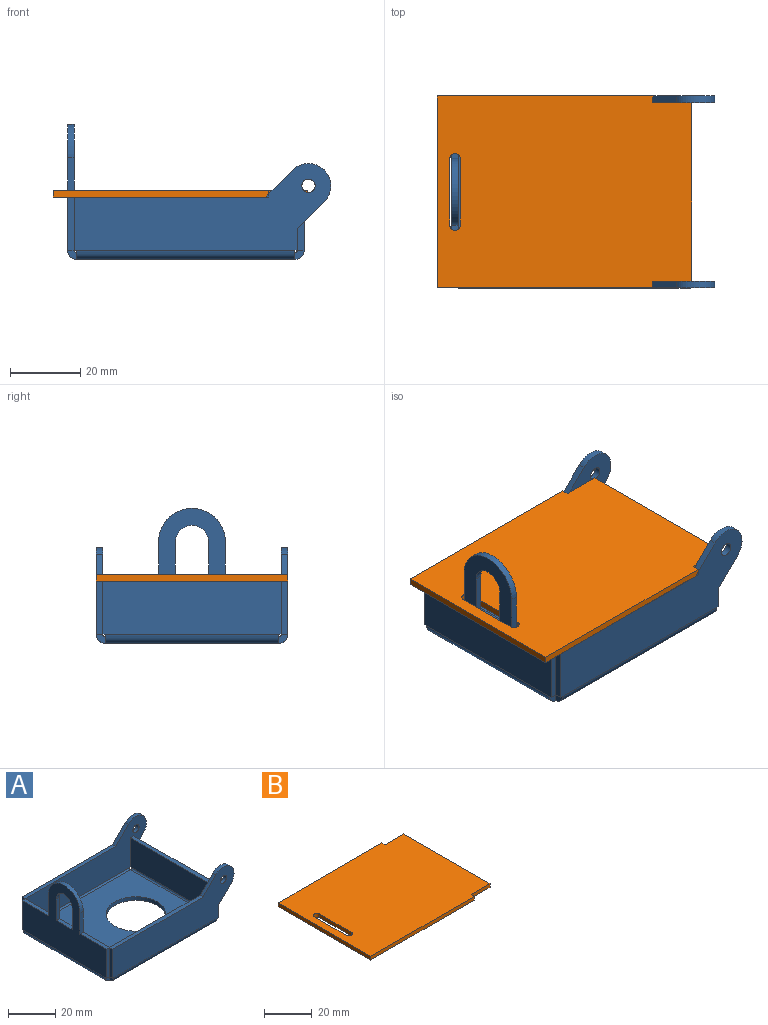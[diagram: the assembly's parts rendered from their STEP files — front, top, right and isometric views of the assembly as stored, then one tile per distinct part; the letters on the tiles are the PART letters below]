
ASSEMBLY  parts=2 mates=1
PART A: 65 faces, bbox 74.9x54.6x38.4 mm
  f0: plane 1.91x0.71mm, normal (0,0,-1), area 1.4mm2, adj f6,f13,f14,f62
  f1: plane 15.85x1.91mm, normal (0,0,1), area 30.2mm2, adj f2,f12,f13,f14
  f2: plane 11.13x1.91mm, normal (0,-1,0), area 21.2mm2, adj f1,f3,f13,f14
  f3: cylinder r=9.53mm len=19.05mm, axis (1,0,0), area 57mm2, adj f2,f4,f13,f14
  f4: plane 11.13x1.91mm, normal (0,1,0), area 21.2mm2, adj f3,f5,f13,f14
  f5: plane 15.85x1.91mm, normal (0,0,1), area 30.2mm2, adj f4,f6,f13,f14
  f6: plane 15.14x1.91mm, normal (0,1,0), area 28.8mm2, adj f0,f5,f13,f14
  f7: plane 1.91x0.71mm, normal (0,0,-1), area 1.4mm2, adj f12,f13,f14,f61
  f8: cylinder r=4.76mm len=9.53mm, axis (1,0,0), area 28.5mm2, adj f9,f11,f13,f14
  f9: plane 11.13x1.91mm, normal (0,1,0), area 21.2mm2, adj f8,f10,f13,f14
  f10: plane 9.53x1.91mm, normal (0,0,1), area 18.1mm2, adj f9,f11,f13,f14
  f11: plane 11.13x1.91mm, normal (0,-1,0), area 21.2mm2, adj f8,f10,f13,f14
  f12: plane 15.14x1.91mm, normal (0,-1,0), area 28.8mm2, adj f1,f7,f13,f14
  f13: plane 50.75x35.79mm, normal (-1,0,0), area 981.1mm2, adj f0,f1,f2,f3,f4,f5,f6,f7
  f14: plane 50.75x35.79mm, normal (1,0,0), area 981.1mm2, adj f0,f1,f2,f3,f4,f5,f6,f7
  f15: cylinder r=12.7mm len=25.4mm, axis (0,0,1), area 152mm2, adj f16,f17
  f16: plane 62.03x49.33mm, normal (0,0,-1), area 2552.9mm2, adj f15,f32,f43,f59,f63
  f17: plane 62.03x49.33mm, normal (0,0,1), area 2552.9mm2, adj f15,f33,f44,f60,f64
  f18: plane 1.91x0.71mm, normal (0,0,-1), area 1.4mm2, adj f23,f28,f29,f31
  f19: plane 1.91x1.16mm, normal (0.8,0,-0.59), area 2.7mm2, adj f20,f26,f28,f29
  f20: cylinder r=6.35mm len=10.84mm, axis (0,1,0), area 34.8mm2, adj f19,f21,f28,f29
  f21: plane 7.67x7.67mm, normal (-0.71,0,0.71), area 20.7mm2, adj f20,f22,f28,f29
  f22: plane 54.47x1.91mm, normal (0,0,1), area 103.8mm2, adj f21,f23,f28,f29
  f23: plane 15.14x1.91mm, normal (-1,0,0), area 28.8mm2, adj f18,f22,f28,f29
  f24: plane 1.91x0.71mm, normal (0,0,-1), area 1.4mm2, adj f25,f28,f29,f30
  f25: plane 6.16x1.91mm, normal (1,0,0), area 11.7mm2, adj f24,f26,f28,f29
  f26: plane 7.82x7.82mm, normal (0.71,0,-0.71), area 21.1mm2, adj f19,f25,f28,f29
  f27: cylinder r=1.91mm len=3.81mm, axis (0,1,0), area 22.8mm2, adj f28,f29
  f28: plane 72.97x24.66mm, normal (0,-1,0), area 1109.8mm2, adj f18,f19,f20,f21,f22,f23,f24,f25
  f29: plane 72.97x24.66mm, normal (0,1,0), area 1109.8mm2, adj f18,f19,f20,f21,f22,f23,f24,f25
  f30: plane 2.64x2.64mm, normal (1,0,0), area 5.1mm2, adj f24,f32,f33,f42
  f31: plane 2.64x2.64mm, normal (-1,0,0), area 5.1mm2, adj f18,f32,f33,f61
  f32: cylinder r=2.64mm len=62.03mm, axis (1,0,0), area 257.4mm2, adj f16,f28,f30,f31
  f33: cylinder r=0.74mm len=62.03mm, axis (1,0,0), area 71.8mm2, adj f17,f29,f30,f31
  f34: plane 1.91x0.71mm, normal (0,0,-1), area 1.4mm2, adj f36,f39,f40,f42
  f35: plane 50.75x1.91mm, normal (0,0,1), area 96.7mm2, adj f36,f38,f39,f40
  f36: plane 15.14x1.91mm, normal (0,-1,0), area 28.8mm2, adj f34,f35,f39,f40
  f37: plane 1.91x0.71mm, normal (0,0,-1), area 1.4mm2, adj f38,f39,f40,f41
  f38: plane 15.14x1.91mm, normal (0,1,0), area 28.8mm2, adj f35,f37,f39,f40
  f39: plane 50.75x15.14mm, normal (1,0,0), area 768.3mm2, adj f34,f35,f36,f37,f38,f43
  f40: plane 50.75x15.14mm, normal (-1,0,0), area 768.3mm2, adj f34,f35,f36,f37,f38,f44
  f41: plane 2.64x2.64mm, normal (0,1,0), area 5.1mm2, adj f37,f43,f44,f58
  f42: plane 2.64x2.64mm, normal (0,-1,0), area 5.1mm2, adj f30,f34,f43,f44
  f43: cylinder r=2.64mm len=49.33mm, axis (0,1,0), area 204.7mm2, adj f16,f39,f41,f42
  f44: cylinder r=0.74mm len=49.33mm, axis (0,1,0), area 57.1mm2, adj f17,f40,f41,f42
  f45: plane 1.91x0.71mm, normal (0,0,-1), area 1.4mm2, adj f47,f55,f56,f58
  f46: plane 7.67x7.67mm, normal (0.71,0,-0.71), area 20.7mm2, adj f47,f53,f55,f56
  f47: plane 6.16x1.91mm, normal (1,0,0), area 11.7mm2, adj f45,f46,f55,f56
  f48: plane 1.91x0.71mm, normal (0,0,-1), area 1.4mm2, adj f49,f55,f56,f57
  f49: plane 15.14x1.91mm, normal (-1,0,0), area 28.8mm2, adj f48,f50,f55,f56
  f50: plane 54.47x1.91mm, normal (0,0,1), area 103.8mm2, adj f49,f51,f55,f56
  f51: plane 7.67x7.67mm, normal (-0.71,0,0.71), area 20.7mm2, adj f50,f52,f55,f56
  f52: cylinder r=6.35mm len=10.84mm, axis (0,-1,0), area 34.8mm2, adj f51,f53,f55,f56
  f53: plane 1.91x1.32mm, normal (0.79,0,-0.61), area 3.2mm2, adj f46,f52,f55,f56
  f54: cylinder r=1.91mm len=3.81mm, axis (0,-1,0), area 22.8mm2, adj f55,f56
  f55: plane 72.97x24.66mm, normal (0,1,0), area 1109.7mm2, adj f45,f46,f47,f48,f49,f50,f51,f52
  f56: plane 72.97x24.66mm, normal (0,-1,0), area 1109.7mm2, adj f45,f46,f47,f48,f49,f50,f51,f52
  f57: plane 2.64x2.64mm, normal (-1,0,0), area 5.1mm2, adj f48,f59,f60,f62
  f58: plane 2.64x2.64mm, normal (1,0,0), area 5.1mm2, adj f41,f45,f59,f60
  f59: cylinder r=2.64mm len=62.03mm, axis (-1,0,0), area 257.4mm2, adj f16,f55,f57,f58
  f60: cylinder r=0.74mm len=62.03mm, axis (-1,0,0), area 71.8mm2, adj f17,f56,f57,f58
  f61: plane 2.64x2.64mm, normal (0,-1,0), area 5.1mm2, adj f7,f31,f63,f64
  f62: plane 2.64x2.64mm, normal (0,1,0), area 5.1mm2, adj f0,f57,f63,f64
  f63: cylinder r=2.64mm len=49.33mm, axis (0,-1,0), area 204.7mm2, adj f13,f16,f61,f62
  f64: cylinder r=0.74mm len=49.33mm, axis (0,-1,0), area 57.1mm2, adj f14,f17,f61,f62
PART B: 14 faces, bbox 72.4x54.6x1.9 mm
  f0: cylinder r=1.52mm len=3.05mm, axis (0,0,-1), area 9.1mm2, adj f1,f11,f12,f13
  f1: plane 18.8x1.91mm, normal (-1,0,0), area 35.8mm2, adj f0,f2,f12,f13
  f2: cylinder r=1.52mm len=3.05mm, axis (0,0,-1), area 9.1mm2, adj f1,f11,f12,f13
  f3: plane 1.91x1.91mm, normal (1,0,0), area 3.6mm2, adj f4,f10,f12,f13
  f4: plane 61.32x1.91mm, normal (0,1,0), area 116.8mm2, adj f3,f5,f12,f13
  f5: plane 54.61x1.91mm, normal (-1,0,0), area 104mm2, adj f4,f6,f12,f13
  f6: plane 61.32x1.91mm, normal (0,-1,0), area 116.8mm2, adj f5,f7,f12,f13
  f7: plane 1.91x1.91mm, normal (1,0,0), area 3.6mm2, adj f6,f8,f12,f13
  f8: plane 11.07x1.91mm, normal (0,-1,0), area 21.1mm2, adj f7,f9,f12,f13
  f9: plane 50.8x1.91mm, normal (1,0,0), area 96.8mm2, adj f8,f10,f12,f13
  f10: plane 11.07x1.91mm, normal (0,1,0), area 21.1mm2, adj f3,f9,f12,f13
  f11: plane 18.8x1.91mm, normal (1,0,0), area 35.8mm2, adj f0,f2,f12,f13
  f12: plane 72.39x54.61mm, normal (0,0,1), area 3846.4mm2, adj f0,f1,f2,f3,f4,f5,f6,f7
  f13: plane 72.39x54.61mm, normal (0,0,-1), area 3846.4mm2, adj f0,f1,f2,f3,f4,f5,f6,f7
PLACE A at identity
PLACE B rot(axis=(0,0,-1),0deg) t=(83.53,-53.81,15.88)mm
MATE fastened B.f13 <-> A.f10  axis (0,0,1) through (13.46,-41.27,15.88)mm
